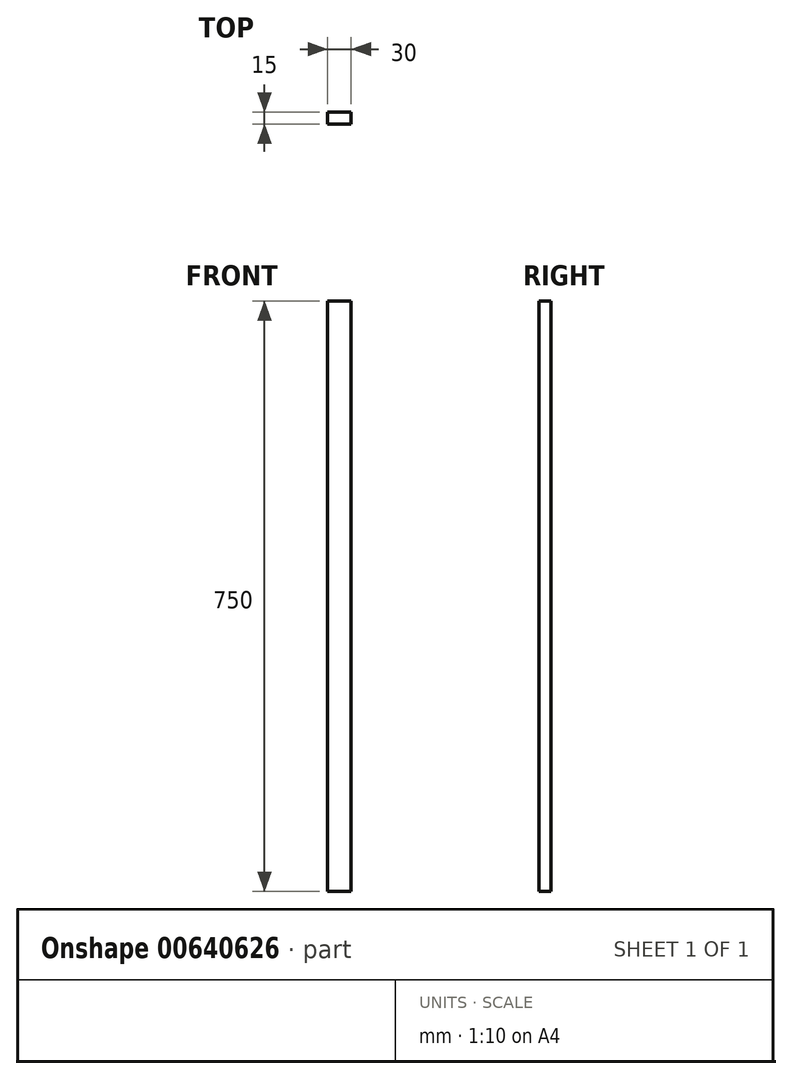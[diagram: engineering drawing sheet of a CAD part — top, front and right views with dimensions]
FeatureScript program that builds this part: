
annotation { "Feature Type Name" : "Feature", "Feature Type Description" : "" }
export const myFeature = defineFeature(function(context is Context, id is Id, definition is map)
    precondition{}
    {
        {
            var Q0;
            Q0=qCreatedBy(makeId("Front.planeOp"),FACE);
            var sketch = newSketch(context, id + "F0", { "sketchPlane" : qUnion([Q0])});
            skLineSegment(sketch, "E0.bottom", {"start": v(0, 0) * mm, "end": v(-30, 0) * mm});
            skLineSegment(sketch, "E0.top", {"start": v(0, 750) * mm, "end": v(-30, 750) * mm});
            skLineSegment(sketch, "E0.left", {"start": v(0, 0) * mm, "end": v(0, 750) * mm});
            skLineSegment(sketch, "E0.right", {"start": v(-30, 0) * mm, "end": v(-30, 750) * mm});
            skSolve(sketch);
        }
        {
            var Q0;
            Q0 = qSketchRegion(id + "F0", true);
            extrude(context, id + "F1", {"entities" : qUnion([Q0]), "depth" : 15 * mm, "offsetDistance" : 25 * mm});
        }
    });
